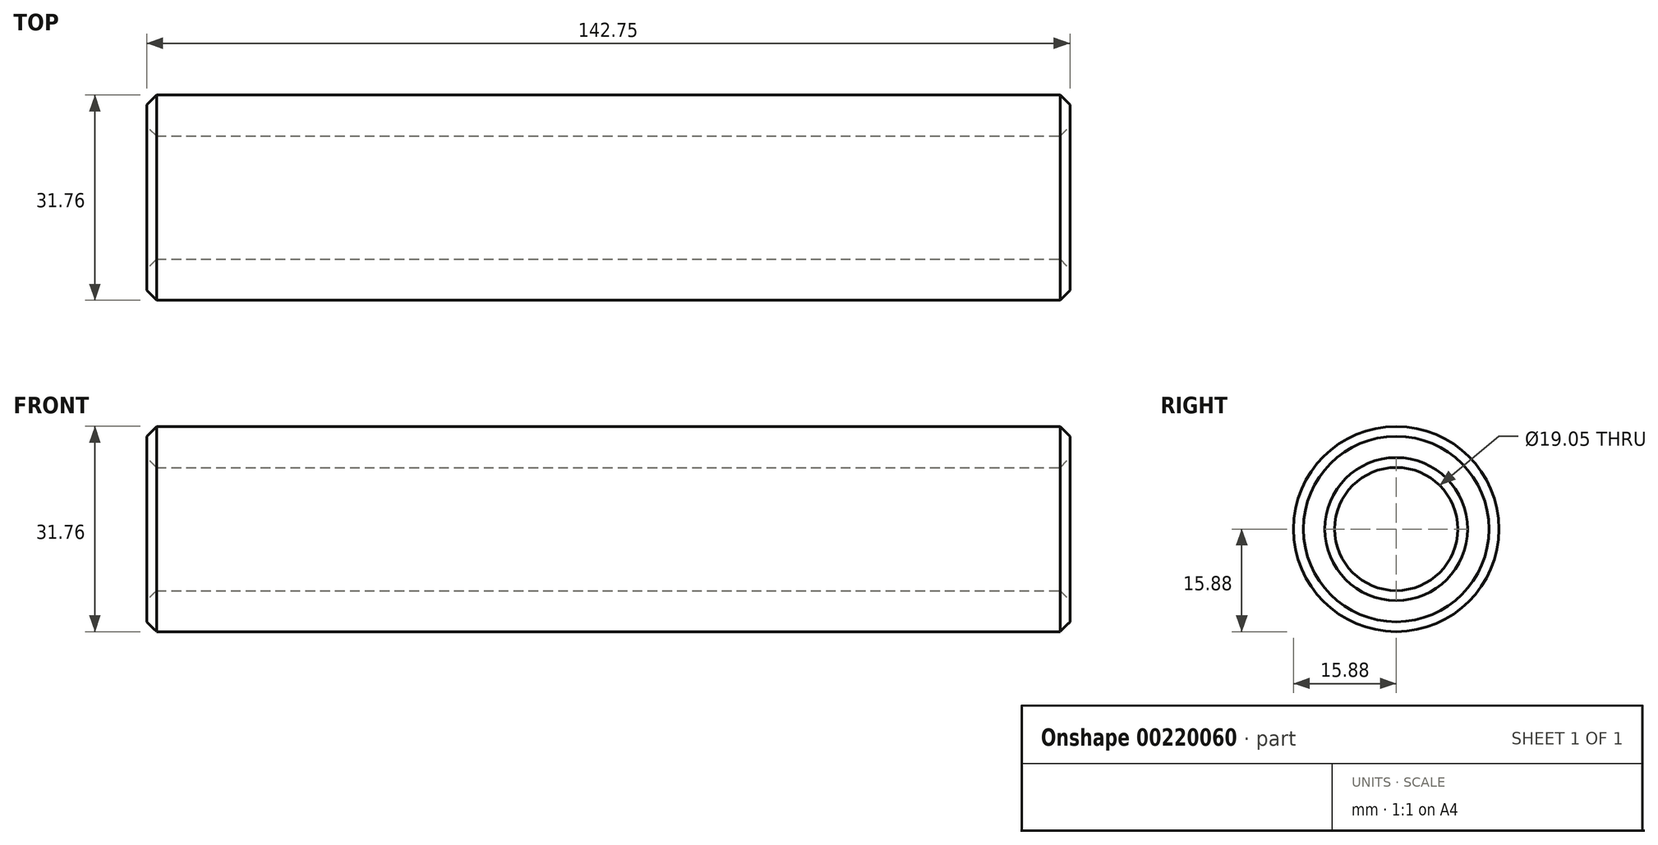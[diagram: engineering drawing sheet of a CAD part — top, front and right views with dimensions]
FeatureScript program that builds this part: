
annotation { "Feature Type Name" : "Feature", "Feature Type Description" : "" }
export const myFeature = defineFeature(function(context is Context, id is Id, definition is map)
    precondition{}
    {
        {
            var Q0;
            Q0=qCreatedBy(makeId("Right.planeOp"),FACE);
            var sketch = newSketch(context, id + "F0", { "sketchPlane" : qUnion([Q0])});
            skCircle(sketch, "E0", {"center": v(0, 0) * mm, "radius": 15.88 * mm});
            skCircle(sketch, "E1", {"center": v(0, 0) * mm, "radius": 9.53 * mm});
            skSolve(sketch);
        }
        {
            var Q0;
            Q0 = qSketchRegion(id + "F0", true);
            extrude(context, id + "F1", {"entities" : qUnion([Q0]), "oppositeDirection" : true, "depth" : 142.75 * mm});
        }
        {
            var Q0;
            Q0=makeQuery(id+"F1.opExtrude","CAP_EDGE",EDGE,{"disambiguationData":[OSD([sQuery(id+"F0.wireOp",EDGE,"E0")])],"isStart":true});
            var Q1;
            Q1=makeQuery(id+"F1.opExtrude","CAP_EDGE",EDGE,{"disambiguationData":[OSD([sQuery(id+"F0.wireOp",EDGE,"E0")])],"isStart":false});
            var Q2;
            Q2=makeQuery(id+"F1.opExtrude","CAP_EDGE",EDGE,{"disambiguationData":[OSD([sQuery(id+"F0.wireOp",EDGE,"E1")])],"isStart":false});
            var Q3;
            Q3=makeQuery(id+"F1.opExtrude","CAP_EDGE",EDGE,{"disambiguationData":[OSD([sQuery(id+"F0.wireOp",EDGE,"E1")])],"isStart":true});
            chamfer(context, id + "F2", {"entities" : qUnion([Q0, Q1, Q2, Q3]), "width" : 1.52 * mm, "tangentPropagation" : true});
        }
    });
